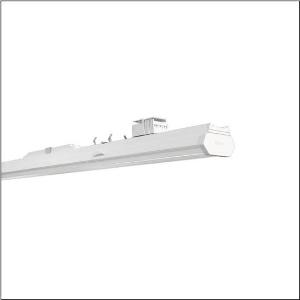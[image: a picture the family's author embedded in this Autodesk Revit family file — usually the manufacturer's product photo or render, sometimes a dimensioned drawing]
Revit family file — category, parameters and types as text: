
# Revit family: licross_21_protected_ho_52tp12mn4e5m
name_source: partatom
category: Lighting Fixtures
units: mm (PartAtom-declared; Revit-internal decimal feet)

## family parameters
Cut with Voids When Loaded = No
Host = Face
Light Source = No
Part Type = Normal
Room Calculation Point = No
Round Connector Dimension = Use Diameter
Shared = No

## types (1)
- --- (1 x LED, 14780 lm, 83.2 W, 4000K)
    Apparent Load = 83 VA
    CIE Flux Codes = 70 91 97 98 100
    Color Rendering = 80
    Color Temperature = 4000K
    Default Elevation = 1800 mm
    Description = Licross 21 Protected HO, luminaire insert, of sheet steel, galvanised, coil coated, white, length: 1.500mm, width: 90mm, height: 101mm, LED rated luminous flux: 14.790lm, light colour: 840, SDCM (Standard Deviation of Colour Matching)MacAdam ≤ 3 SDCM (initial), control gear: ON/OFF Multilumen, with plug, 3-pole, with phase selection, mains connection: 220..240V, AC, 50/60Hz, rated input power: 83W, internal wiring halogen-free, primary light control with lens, of plastic, primary optical cover: cover, of PMMA, light emission: direct distribution, primary light characteristic: symmetric, protection rating (complete): IP64, insulation class (complete): insulation class I (protective earthing), certification: CE, ENEC, VDE, UKCA, protection symbol: D if used in an environment with conductive dust loads with corresponding accessories, impact resistance: IK06, permissible ambient temperature for indoor applications: -35..+35°C, corresponds to IFS (International Featured Standards) requirements for safety and quality in the food industry, reducing of maximum allowable ambient temperature of 5°C with ceiling mounting, LABS conformity tested according to VDMA 24364:2018-05, The light source and the operating device comply with the requirements of the Ecodesign Regulation (EU) 2019/2020 and are replaceable in accordance with this regulation, packaging unit: 1 piece
    Height = 92 mm
    Lamp = 1 x LED
    Lamp Light Flux = 14780 lm
    Lamp Power = 83.2 W
    Lamp count = 1
    Length = 1500 mm
    Luminous efficacy = 178 lm/W
    Manufacturer = Siteco
    ModVariant = No
    Model = 52TP12MN4E5M
    Mounting Place = Ceiling
    Mounting Type = Pendant
    Number of Poles = 1
    OnlyDefault = Yes
    Power Factor = 1
    Product Name = Licross 21 Protected HO
    Product group = luminaire insert | ceiling pendant
    ProductGroupID = 901
    Protection Class = Protection class I
    Protection Degree = IP 64
    RLX_Detail_Level = 1
    RLX_Emergency_Light_Flux = 0 lm
    RLX_Emergency_Type = 0
    RLX_Emergency_Type_DB = No
    RlxData = <blob elided: 22253 chars, md5=b25b722b>
    Socket = socket
    Standby Power = 0 W
    System Light Flux = 14780 lm
    System Power = 83 W
    Type Comments = factory setting: luminous flux: 100 % | (A | C | E) | 195 mA
    Type Image = l_1256148.jpg
    URL = http://relux.com
    VarID = @adj_110659
    Voltage = 0 V
    Weight = 0.00 kg
    Width = 88 mm

## geometry (parser evidence)
native form markers: Blend x4, Sweep x10
no freeform markers — native parametric forms only
